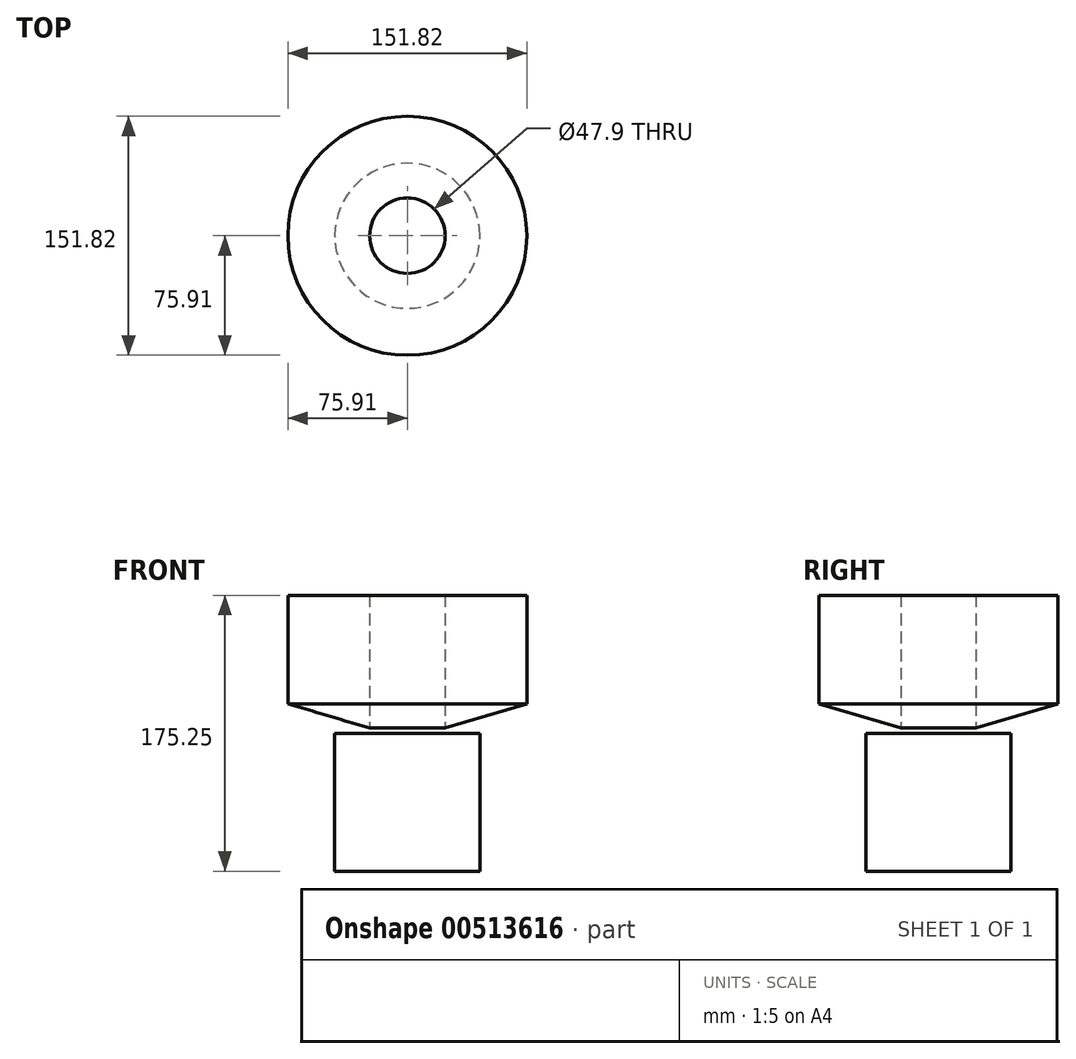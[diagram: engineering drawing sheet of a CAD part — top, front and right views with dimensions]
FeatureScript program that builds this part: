
annotation { "Feature Type Name" : "Feature", "Feature Type Description" : "" }
export const myFeature = defineFeature(function(context is Context, id is Id, definition is map)
    precondition{}
    {
        {
            var Q0;
            Q0=qCreatedBy(makeId("Top.planeOp"),FACE);
            var sketch = newSketch(context, id + "F0", { "sketchPlane" : qUnion([Q0])});
            skCircle(sketch, "E0", {"center": v(0, 0) * mm, "radius": 46.1 * mm});
            skSolve(sketch);
        }
        {
            var Q0;
            Q0=makeQuery(id+"F0.imprint","IMPRINT",FACE,{"disambiguationData":[TD([[makeQuery(id+"F0.imprint","IMPRINT",EDGE,{"derivedFrom":sQuery(id+"F0.wireOp",EDGE,"E0")}),1.0]])]});
            extrude(context, id + "F1", {"entities" : qUnion([Q0]), "depth" : 87.63 * mm});
        }
        {
            var Q0;
            Q0=qCreatedBy(makeId("Front.planeOp"),FACE);
            var sketch = newSketch(context, id + "F2", { "sketchPlane" : qUnion([Q0])});
            skLineSegment(sketch, "E1", {"start": v(23.95, 90.9) * mm, "end": v(23.95, 175.25) * mm});
            skLineSegment(sketch, "E2", {"start": v(23.95, 175.25) * mm, "end": v(75.9, 175.25) * mm});
            skLineSegment(sketch, "E3", {"start": v(75.9, 175.25) * mm, "end": v(75.9, 106.42) * mm});
            skLineSegment(sketch, "E4", {"start": v(75.9, 106.42) * mm, "end": v(23.95, 90.9) * mm});
            skLineSegment(sketch, "E5", {"start": v(0, 0) * mm, "end": v(0, 194.14) * mm, "construction": true});
            skSolve(sketch);
        }
        {
            var Q0;
            Q0 = qSketchRegion(id + "F2", true);
            var Q1;
            Q1=sQuery(id+"F2.wireOp",EDGE,"E5");
            revolve(context, id + "F3", {"entities" : qUnion([Q0]), "axis" : qUnion([Q1]), "revolveType" : RevolveType.FULL});
        }
    });
